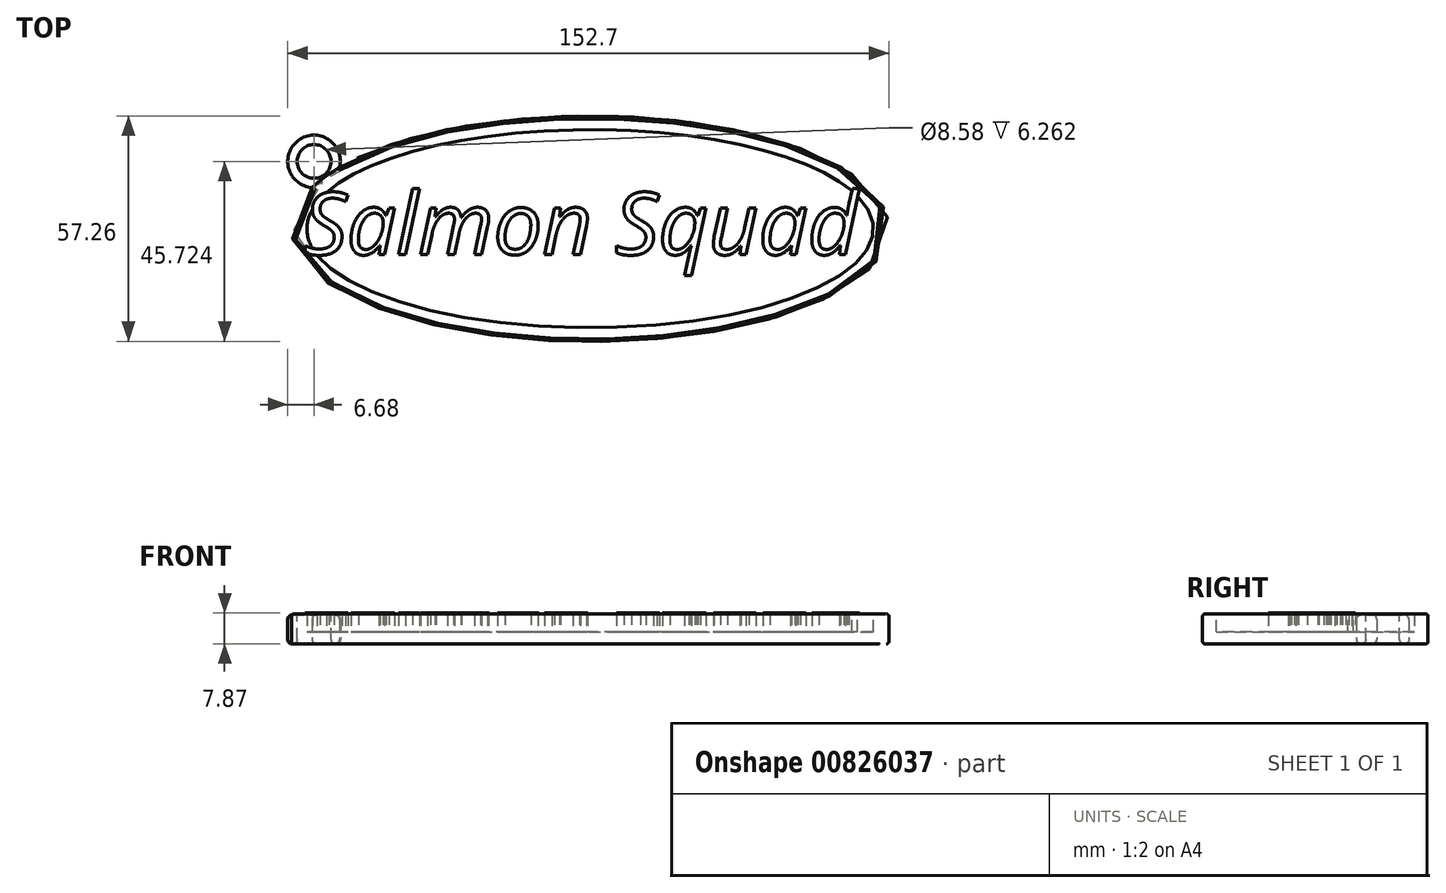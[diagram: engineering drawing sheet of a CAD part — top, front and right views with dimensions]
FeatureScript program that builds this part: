
annotation { "Feature Type Name" : "Feature", "Feature Type Description" : "" }
export const myFeature = defineFeature(function(context is Context, id is Id, definition is map)
    precondition{}
    {
        {
            var Q0;
            Q0=qCreatedBy(makeId("Top.planeOp"),FACE);
            var sketch = newSketch(context, id + "F0", { "sketchPlane" : qUnion([Q0])});
            skEllipse(sketch, "E0", {"center": v(0, 0) * mm, "majorRadius": 75.87 * mm, "minorRadius": 28.63 * mm, "majorAxis": v(1, 0)});
            skSolve(sketch);
        }
        {
            var Q0;
            Q0=makeQuery(id+"F0.imprint","IMPRINT",FACE,{"disambiguationData":[TD([[makeQuery(id+"F0.imprint","IMPRINT",EDGE,{"derivedFrom":sQuery(id+"F0.wireOp",EDGE,"E0")}),1.0]])]});
            extrude(context, id + "F1", {"entities" : qUnion([Q0]), "depth" : 7.62 * mm, "offsetDistance" : 25.4 * mm});
        }
        {
            var Q0;
            Q0=makeQuery(id+"F1.opExtrude","CAP_FACE",FACE,{"disambiguationData":[OSD([sQuery(id+"F0.wireOp",EDGE,"E0")])],"isStart":false});
            var sketch = newSketch(context, id + "F2", { "sketchPlane" : qUnion([Q0])});
            skEllipse(sketch, "E1", {"center": v(0, 0) * mm, "majorRadius": 71.98 * mm, "minorRadius": 25.15 * mm, "majorAxis": v(1, 0)});
            skSolve(sketch);
        }
        {
            var Q0;
            Q0 = qSketchRegion(id + "F2", true);
            extrude(context, id + "F3", {"entities" : qUnion([Q0]), "operationType" : NewBodyOperationType.REMOVE, "oppositeDirection" : true, "depth" : 4.57 * mm, "offsetDistance" : 25.4 * mm});
        }
        {
            var Q0;
            Q0=makeQuery(id+"F3.boolean.opBoolean","COPY",FACE,{"derivedFrom":makeQuery(id+"F3.opExtrude","CAP_FACE",FACE,{"disambiguationData":[OSD([sQuery(id+"F2.wireOp",EDGE,"E1")])],"isStart":false})});
            var sketch = newSketch(context, id + "F4", { "sketchPlane" : qUnion([Q0])});
            skText(sketch, "E2", { "text": "Salmon Squad \n", "fontName": "OpenSans-Italic.ttf"});
            const initialGuessF4  = {"E2": [-0.07288, -0.00657, 1, 0, 0.01587]};
            skSetInitialGuess(sketch, initialGuessF4);
            skSolve(sketch);
        }
        {
            var Q0;
            Q0 = qSketchRegion(id + "F4", true);
            extrude(context, id + "F5", {"entities" : qUnion([Q0]), "operationType" : NewBodyOperationType.ADD, "depth" : 4.83 * mm, "offsetDistance" : 25.4 * mm});
        }
        {
            var Q0;
            Q0=qCreatedBy(makeId("Top.planeOp"),FACE);
            var sketch = newSketch(context, id + "F6", { "sketchPlane" : qUnion([Q0])});
            skCircle(sketch, "E3", {"center": v(-70.15, 17.1) * mm, "radius": 6.68 * mm});
            skSolve(sketch);
        }
        {
            var Q0;
            Q0=makeQuery(id+"F6.imprint","IMPRINT",FACE,{"disambiguationData":[TD([[makeQuery(id+"F6.imprint","IMPRINT",EDGE,{"derivedFrom":sQuery(id+"F6.wireOp",EDGE,"E3")}),1.0]])]});
            extrude(context, id + "F7", {"entities" : qUnion([Q0]), "operationType" : NewBodyOperationType.ADD, "depth" : 7.37 * mm, "offsetDistance" : 25.4 * mm});
        }
        {
            var Q0;
            Q0=makeQuery(id+"F7.opExtrude","CAP_FACE",FACE,{"disambiguationData":[OSD([sQuery(id+"F6.wireOp",EDGE,"E3")])],"isStart":false});
            var sketch = newSketch(context, id + "F8", { "sketchPlane" : qUnion([Q0])});
            skCircle(sketch, "E4", {"center": v(-70.15, 17.1) * mm, "radius": 4.3 * mm});
            skSolve(sketch);
        }
        {
            var Q0;
            Q0=makeQuery(id+"F8.imprint","IMPRINT",FACE,{"disambiguationData":[TD([[makeQuery(id+"F8.imprint","IMPRINT",EDGE,{"derivedFrom":sQuery(id+"F8.wireOp",EDGE,"E4")}),1.0]])]});
            extrude(context, id + "F9", {"entities" : qUnion([Q0]), "operationType" : NewBodyOperationType.REMOVE, "oppositeDirection" : true, "depth" : 25.4 * mm, "offsetDistance" : 25.4 * mm});
        }
        {
            var Q0;
            Q0=makeQuery(id+"F7.opExtrude","CAP_EDGE",EDGE,{"disambiguationData":[OSD([sQuery(id+"F6.wireOp",EDGE,"E3")])],"isStart":false});
            var Q1;
            Q1=makeQuery(id+"F9.boolean.opBoolean","COPY",EDGE,{"derivedFrom":makeQuery(id+"F9.opExtrude","CAP_EDGE",EDGE,{"disambiguationData":[OSD([sQuery(id+"F8.wireOp",EDGE,"E4")])],"isStart":true})});
            var Q2;
            Q2=makeQuery(id+"F7.opExtrude","CAP_EDGE",EDGE,{"disambiguationData":[OSD([sQuery(id+"F6.wireOp",EDGE,"E3")])],"isStart":true});
            var Q3;
            Q3=makeQuery(id+"F9.boolean.opBoolean","INTERSECT",EDGE,{"derivedFrom":[makeQuery(id+"F7.boolean.opBoolean","MERGE",FACE,{"derivedFrom":[makeQuery(id+"F1.opExtrude","CAP_FACE",FACE,{"disambiguationData":[OSD([sQuery(id+"F0.wireOp",EDGE,"E0")])],"isStart":true}),makeQuery(id+"F7.opExtrude","CAP_FACE",FACE,{"disambiguationData":[OSD([sQuery(id+"F6.wireOp",EDGE,"E3")])],"isStart":true})]}),makeQuery(id+"F9.opExtrude","SWEPT_FACE",FACE,{"disambiguationData":[OSD([sQuery(id+"F8.wireOp",EDGE,"E4")])]})]});
            fillet(context, id + "F10", {"entities" : qUnion([Q0, Q1, Q2, Q3]), "radius" : 1.1 * mm, "tangentPropagation" : true, "allowEdgeOverflow" : false});
        }
        {
            var Q0;
            Q0=makeQuery(id+"F1.opExtrude","CAP_EDGE",EDGE,{"disambiguationData":[OSD([sQuery(id+"F0.wireOp",EDGE,"E0")])],"isStart":true});
            var Q1;
            Q1=makeQuery(id+"F1.opExtrude","CAP_EDGE",EDGE,{"disambiguationData":[OSD([sQuery(id+"F0.wireOp",EDGE,"E0")])],"isStart":false});
            fillet(context, id + "F11", {"entities" : qUnion([Q0, Q1]), "radius" : 0.61 * mm, "tangentPropagation" : true, "allowEdgeOverflow" : false});
        }
    });
